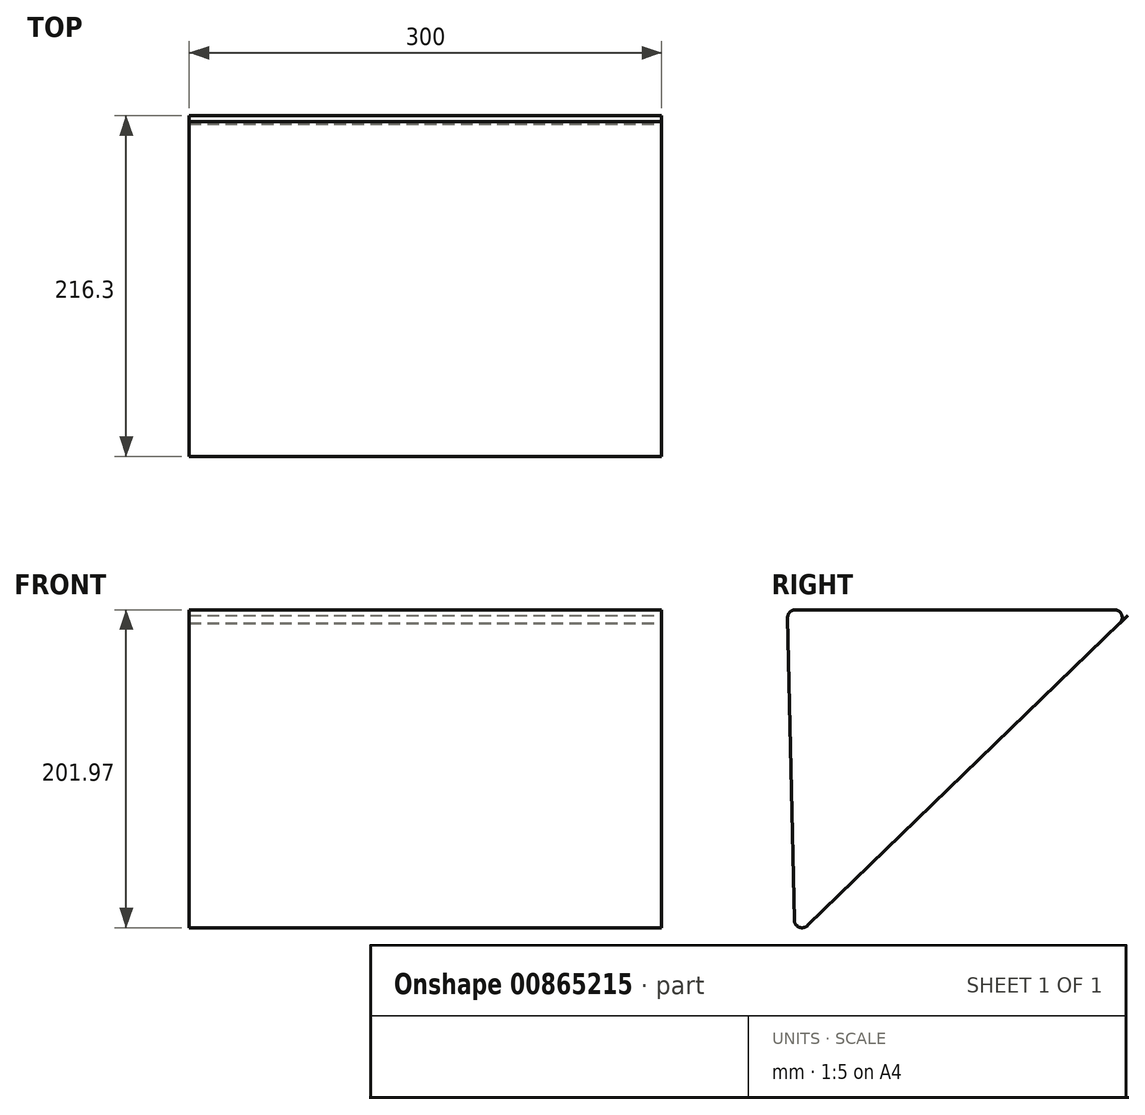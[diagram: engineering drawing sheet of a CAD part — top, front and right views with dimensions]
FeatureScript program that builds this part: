
annotation { "Feature Type Name" : "Feature", "Feature Type Description" : "" }
export const myFeature = defineFeature(function(context is Context, id is Id, definition is map)
    precondition{}
    {
        {
            var Q0;
            Q0=qCreatedBy(makeId("Right.planeOp"),FACE);
            var sketch = newSketch(context, id + "F0", { "sketchPlane" : qUnion([Q0])});
            skLineSegment(sketch, "E0", {"start": v(-69.1, 0) * mm, "end": v(133.45, 0) * mm});
            skLineSegment(sketch, "E1", {"start": v(-336.17, 0) * mm, "end": v(-335.51, 0.75) * mm});
            skLineSegment(sketch, "E2", {"start": v(-74.1, -5.11) * mm, "end": v(-69.84, -197.08) * mm});
            skLineSegment(sketch, "E3", {"start": v(142.2, -3.48) * mm, "end": v(136.93, -8.59) * mm});
            skLineSegment(sketch, "E4", {"start": v(-61.36, -200.56) * mm, "end": v(142.2, -3.48) * mm});
            skPoint(sketch, "E5.visualSharp", {"position": v(145.79, 0) * mm});
            skArc(sketch, "E5.filletArc", {"start": v(136.93, -8.59) * mm, "mid": v(138.08, -3.12) * mm, "end": v(133.45, 0) * mm});
            skPoint(sketch, "E6.visualSharp", {"position": v(-74.21, 0) * mm});
            skArc(sketch, "E6.filletArc", {"start": v(-69.1, 0) * mm, "mid": v(-72.68, -1.5) * mm, "end": v(-74.1, -5.11) * mm});
            skPoint(sketch, "E7.visualSharp", {"position": v(-69.58, -208.52) * mm});
            skArc(sketch, "E7.filletArc", {"start": v(-69.84, -197.08) * mm, "mid": v(-66.74, -201.6) * mm, "end": v(-61.36, -200.56) * mm});
            skSolve(sketch);
        }
        {
            var Q0;
            Q0 = qSketchRegion(id + "F0", true);
            extrude(context, id + "F1", {"entities" : qUnion([Q0]), "oppositeDirection" : true, "depth" : 300 * mm, "offsetDistance" : 25 * mm});
        }
    });
